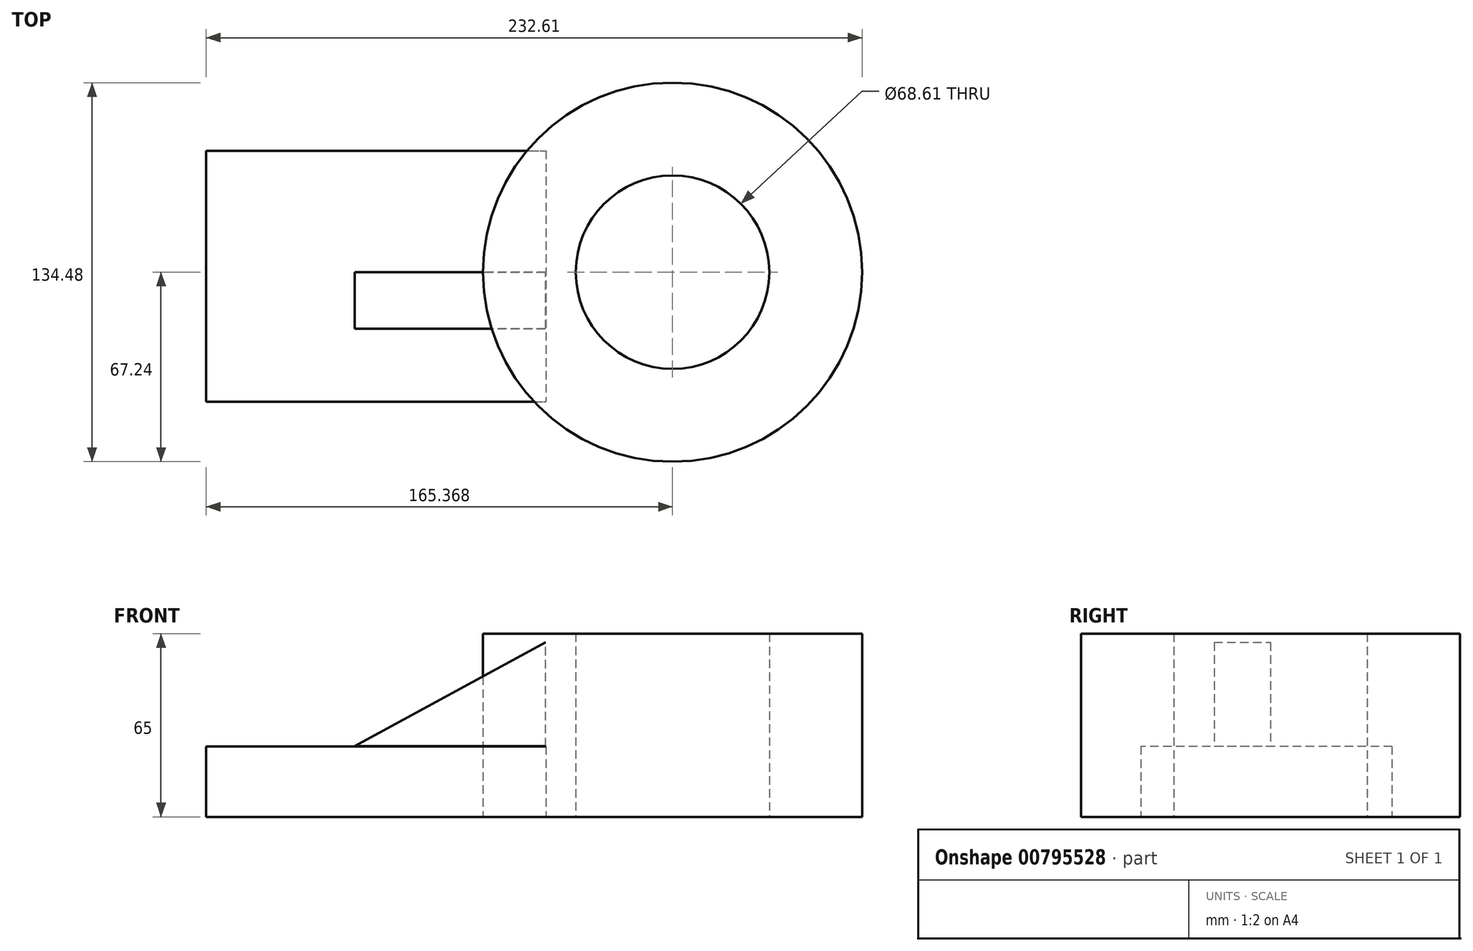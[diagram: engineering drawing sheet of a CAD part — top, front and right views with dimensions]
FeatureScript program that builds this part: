
annotation { "Feature Type Name" : "Feature", "Feature Type Description" : "" }
export const myFeature = defineFeature(function(context is Context, id is Id, definition is map)
    precondition{}
    {
        {
            var Q0;
            Q0=qCreatedBy(makeId("Top.planeOp"),FACE);
            var sketch = newSketch(context, id + "F0", { "sketchPlane" : qUnion([Q0])});
            skLineSegment(sketch, "E0.bottom", {"start": v(-124.7, 43.1) * mm, "end": v(-4.17, 43.1) * mm});
            skLineSegment(sketch, "E0.top", {"start": v(-124.7, -45.98) * mm, "end": v(-4.17, -45.98) * mm});
            skLineSegment(sketch, "E0.left", {"start": v(-124.7, 43.1) * mm, "end": v(-124.7, -45.98) * mm});
            skLineSegment(sketch, "E0.right", {"start": v(-4.17, 43.1) * mm, "end": v(-4.17, -45.98) * mm});
            skSolve(sketch);
        }
        {
            var Q0;
            Q0 = qSketchRegion(id + "F0", true);
            extrude(context, id + "F1", {"entities" : qUnion([Q0]), "depth" : 25 * mm, "offsetDistance" : 25 * mm});
        }
        {
            var Q0;
            Q0=qCreatedBy(makeId("Front.planeOp"),FACE);
            var sketch = newSketch(context, id + "F2", { "sketchPlane" : qUnion([Q0])});
            skLineSegment(sketch, "E1", {"start": v(-72.01, 25.07) * mm, "end": v(-4.31, 25.07) * mm});
            skLineSegment(sketch, "E2", {"start": v(-4.31, 25.07) * mm, "end": v(-4.31, 61.9) * mm});
            skLineSegment(sketch, "E3", {"start": v(-4.31, 61.9) * mm, "end": v(-72.01, 25.07) * mm});
            skSolve(sketch);
        }
        {
            var Q0;
            Q0 = qSketchRegion(id + "F2", true);
            extrude(context, id + "F3", {"entities" : qUnion([Q0]), "depth" : 20 * mm, "offsetDistance" : 25 * mm});
        }
        {
            var Q0;
            Q0=qCreatedBy(makeId("Top.planeOp"),FACE);
            var sketch = newSketch(context, id + "F4", { "sketchPlane" : qUnion([Q0])});
            skCircle(sketch, "E4", {"center": v(40.67, 0) * mm, "radius": 67.24 * mm});
            skCircle(sketch, "E5", {"center": v(40.67, 0) * mm, "radius": 34.3 * mm});
            skSolve(sketch);
        }
        {
            var Q0;
            Q0 = qSketchRegion(id + "F4", true);
            extrude(context, id + "F5", {"entities" : qUnion([Q0]), "depth" : 65 * mm, "offsetDistance" : 25 * mm});
        }
    });
